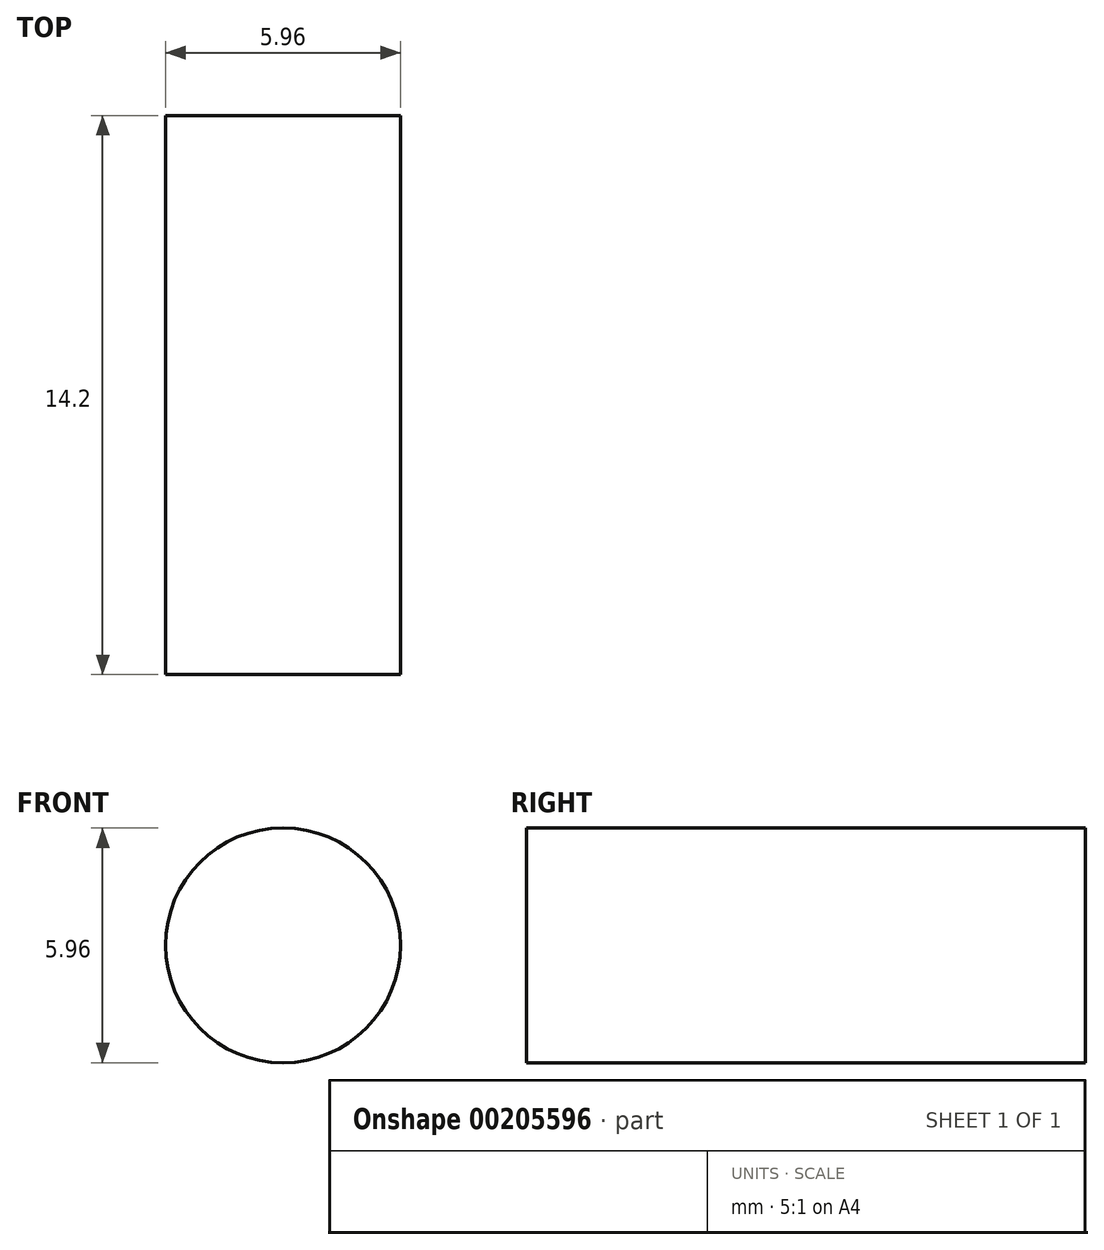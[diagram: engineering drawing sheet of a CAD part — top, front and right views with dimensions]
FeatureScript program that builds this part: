
annotation { "Feature Type Name" : "Feature", "Feature Type Description" : "" }
export const myFeature = defineFeature(function(context is Context, id is Id, definition is map)
    precondition{}
    {
        {
            var Q0;
            Q0=qCreatedBy(makeId("Front.planeOp"),FACE);
            var sketch = newSketch(context, id + "F0", { "sketchPlane" : qUnion([Q0])});
            skCircle(sketch, "E0", {"center": v(0, 0) * mm, "radius": 2.98 * mm});
            skSolve(sketch);
        }
        {
            var Q0;
            Q0=qSketchRegion(id+"F0",true);
            extrude(context, id + "F1", {"entities" : qUnion([Q0]), "depth" : 14.2 * mm});
        }
    });
